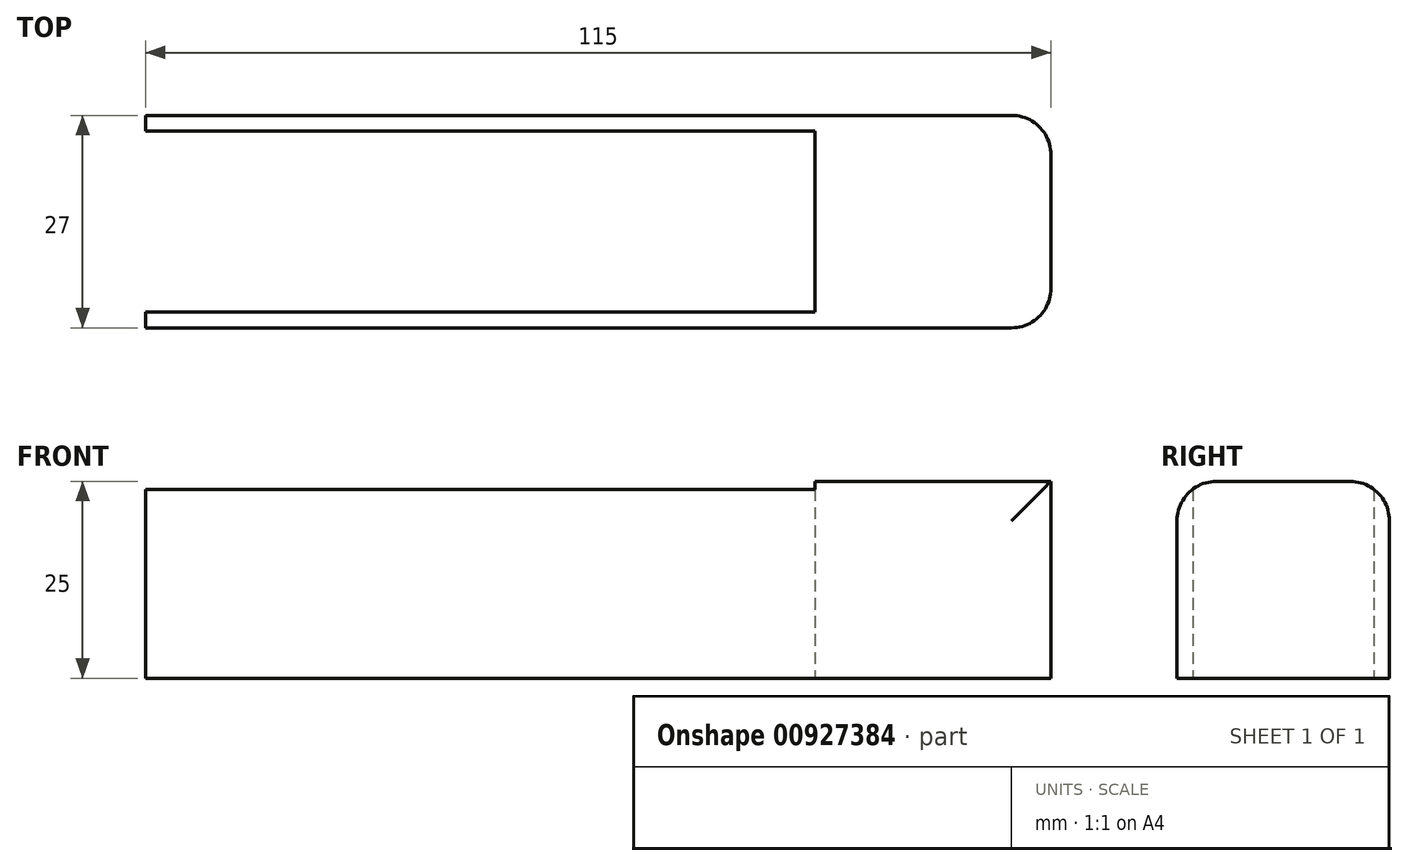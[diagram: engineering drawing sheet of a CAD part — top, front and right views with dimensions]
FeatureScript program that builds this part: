
annotation { "Feature Type Name" : "Feature", "Feature Type Description" : "" }
export const myFeature = defineFeature(function(context is Context, id is Id, definition is map)
    precondition{}
    {
        {
            var Q0;
            Q0=qCreatedBy(makeId("Top.planeOp"),FACE);
            var sketch = newSketch(context, id + "F0", { "sketchPlane" : qUnion([Q0])});
            skLineSegment(sketch, "E0.bottom", {"start": v(16.86, -11.06) * mm, "end": v(46.86, -11.06) * mm});
            skLineSegment(sketch, "E0.top", {"start": v(16.86, 11.94) * mm, "end": v(46.86, 11.94) * mm});
            skLineSegment(sketch, "E0.left", {"start": v(16.86, -11.06) * mm, "end": v(16.86, 11.94) * mm});
            skLineSegment(sketch, "E0.right", {"start": v(46.86, -11.06) * mm, "end": v(46.86, 11.94) * mm});
            skLineSegment(sketch, "E1.bottom", {"start": v(46.86, 11.94) * mm, "end": v(-68.14, 11.94) * mm});
            skLineSegment(sketch, "E1.top", {"start": v(46.86, 13.94) * mm, "end": v(-68.14, 13.94) * mm});
            skLineSegment(sketch, "E1.left", {"start": v(46.86, 11.94) * mm, "end": v(46.86, 13.94) * mm});
            skLineSegment(sketch, "E1.right", {"start": v(-68.14, 11.94) * mm, "end": v(-68.14, 13.94) * mm});
            skLineSegment(sketch, "E2.bottom", {"start": v(46.86, -11.06) * mm, "end": v(-68.14, -11.06) * mm});
            skLineSegment(sketch, "E2.top", {"start": v(46.86, -13.06) * mm, "end": v(-68.14, -13.06) * mm});
            skLineSegment(sketch, "E2.left", {"start": v(46.86, -11.06) * mm, "end": v(46.86, -13.06) * mm});
            skLineSegment(sketch, "E2.right", {"start": v(-68.14, -11.06) * mm, "end": v(-68.14, -13.06) * mm});
            skSolve(sketch);
        }
        {
            var Q0;
            Q0=makeQuery(id+"F0.imprint","IMPRINT",FACE,{"disambiguationData":[TD([[makeQuery(id+"F0.imprint","IMPRINT",EDGE,{"derivedFrom":sQuery(id+"F0.wireOp",EDGE,"E2.top")}),-1.0]])]});
            var Q1;
            Q1=makeQuery(id+"F0.imprint","IMPRINT",FACE,{"disambiguationData":[TD([[makeQuery(id+"F0.imprint","IMPRINT",EDGE,{"derivedFrom":sQuery(id+"F0.wireOp",EDGE,"E1.top")}),1.0]])]});
            var Q2;
            {var subQ0=sQuery(id+"F0.wireOp",EDGE,"E0.left");Q2=makeQuery(id+"F0.imprint","IMPRINT",FACE,{"disambiguationData":[TD([[makeQuery(id+"F0.imprint","IMPRINT",EDGE,{"derivedFrom":subQ0}),-1.0]])]});}
            extrude(context, id + "F1", {"entities" : qUnion([Q0, Q1, Q2]), "depth" : 25 * mm, "offsetDistance" : 25 * mm});
        }
        {
            var Q0;
            Q0=makeQuery(id+"F1.opExtrude","SWEPT_EDGE",EDGE,{"disambiguationData":[OSD([sQuery(id+"F0.wireOp",EDGE,"E2.top"),sQuery(id+"F0.wireOp",EDGE,"E2.left")])]});
            var Q1;
            Q1=makeQuery(id+"F1.opExtrude","SWEPT_EDGE",EDGE,{"disambiguationData":[OSD([sQuery(id+"F0.wireOp",EDGE,"E1.top"),sQuery(id+"F0.wireOp",EDGE,"E1.left")])]});
            var Q2;
            Q2=makeQuery(id+"F1.opExtrude","CAP_EDGE",EDGE,{"disambiguationData":[OSD([sQuery(id+"F0.wireOp",EDGE,"E2.top")])],"isStart":false});
            var Q3;
            Q3=makeQuery(id+"F1.opExtrude","CAP_EDGE",EDGE,{"disambiguationData":[OSD([sQuery(id+"F0.wireOp",EDGE,"E1.top")])],"isStart":false});
            fillet(context, id + "F2", {"entities" : qUnion([Q0, Q1, Q2, Q3]), "radius" : 5 * mm, "tangentPropagation" : true, "allowEdgeOverflow" : false});
        }
    });
